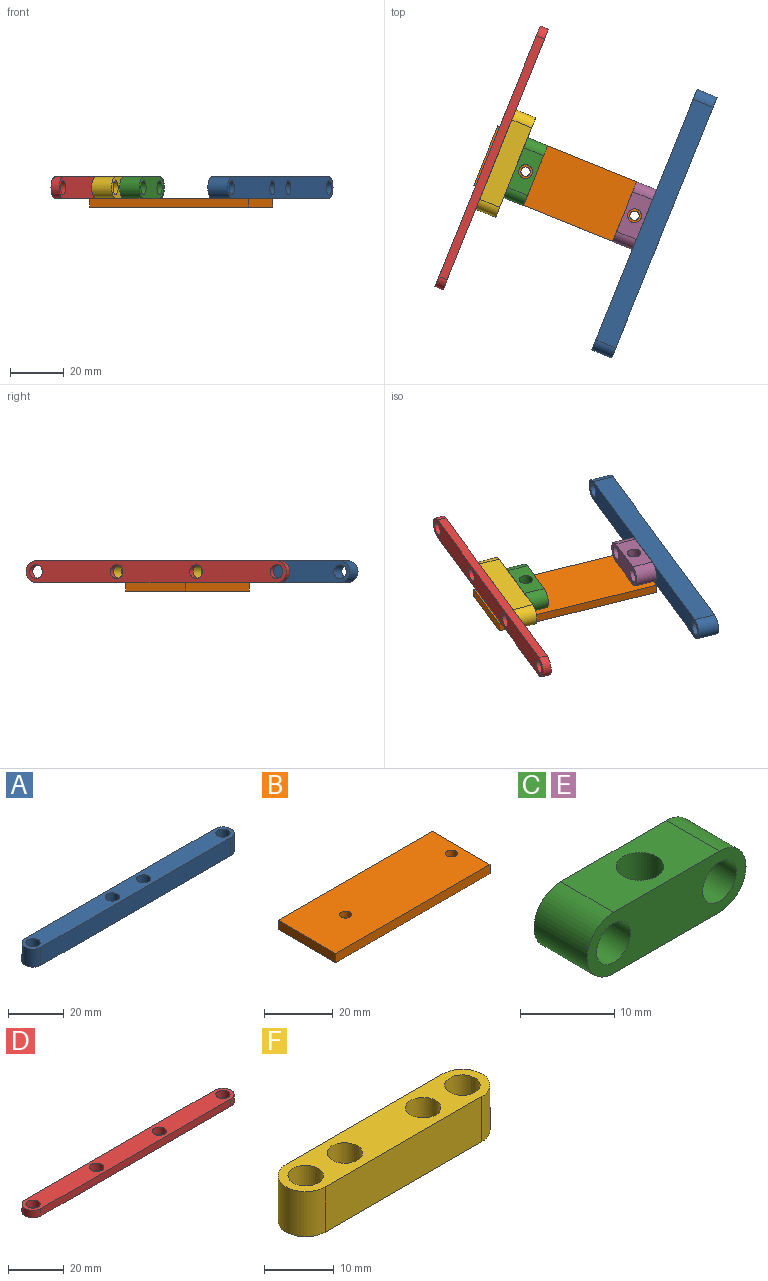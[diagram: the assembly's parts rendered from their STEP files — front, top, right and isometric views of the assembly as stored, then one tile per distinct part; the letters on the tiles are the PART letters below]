
ASSEMBLY  parts=6 mates=14
PART A: 10 faces, bbox 104.1x7.9x7.9 mm
  f0: plane 96.16x7.94mm, normal (0,1,0), area 763.3mm2, adj f6,f7,f8,f9
  f1: plane 96.16x7.94mm, normal (0,-1,0), area 763.3mm2, adj f6,f7,f8,f9
  f2: cylinder r=2.54mm len=7.94mm, axis (0,0,-1), area 126.7mm2, adj f6,f7
  f3: cylinder r=2.54mm len=7.94mm, axis (0,0,-1), area 126.7mm2, adj f6,f7
  f4: cylinder r=2.54mm len=7.94mm, axis (0,0,-1), area 126.7mm2, adj f6,f7
  f5: cylinder r=2.54mm len=7.94mm, axis (0,0,-1), area 126.7mm2, adj f6,f7
  f6: plane 104.1x7.94mm, normal (0,0,1), area 731.7mm2, adj f0,f1,f2,f3,f4,f5,f8,f9
  f7: plane 104.1x7.94mm, normal (0,0,-1), area 731.7mm2, adj f0,f1,f2,f3,f4,f5,f8,f9
  f8: cylinder r=3.97mm len=7.94mm, axis (0,0,-1), area 99mm2, adj f0,f1,f6,f7
  f9: cylinder r=3.97mm len=7.94mm, axis (0,0,-1), area 99mm2, adj f0,f1,f6,f7
PART B: 8 faces, bbox 63.4x23.8x3.3 mm
  f0: plane 63.39x3.25mm, normal (0,1,0), area 206.1mm2, adj f1,f5,f6,f7
  f1: plane 23.81x3.25mm, normal (-1,0,0), area 77.4mm2, adj f0,f2,f6,f7
  f2: plane 63.39x3.25mm, normal (0,-1,0), area 206.1mm2, adj f1,f5,f6,f7
  f3: cylinder r=1.73mm len=3.45mm, axis (0,0,-1), area 35.3mm2, adj f6,f7
  f4: cylinder r=1.73mm len=3.45mm, axis (0,0,-1), area 35.3mm2, adj f6,f7
  f5: plane 23.81x3.25mm, normal (1,0,0), area 77.4mm2, adj f0,f2,f6,f7
  f6: plane 63.39x23.81mm, normal (0,0,1), area 1490.7mm2, adj f0,f1,f2,f3,f4,f5
  f7: plane 63.39x23.81mm, normal (0,0,-1), area 1490.7mm2, adj f0,f1,f2,f3,f4,f5
PART C: 9 faces, bbox 23.8x7.9x7.9 mm
  f0: plane 23.81x7.94mm, normal (0,-1,0), area 135mm2, adj f3,f4,f5,f6,f7,f8
  f1: plane 23.81x7.94mm, normal (0,1,0), area 135mm2, adj f3,f4,f5,f6,f7,f8
  f2: cylinder r=2.54mm len=7.94mm, axis (0,0,-1), area 126.7mm2, adj f3,f4
  f3: plane 15.88x7.94mm, normal (0,0,1), area 105.7mm2, adj f0,f1,f2,f7,f8
  f4: plane 15.88x7.94mm, normal (0,0,-1), area 105.7mm2, adj f0,f1,f2,f7,f8
  f5: cylinder r=2.54mm len=7.94mm, axis (0,-1,0), area 126.7mm2, adj f0,f1
  f6: cylinder r=2.54mm len=7.94mm, axis (0,-1,0), area 126.7mm2, adj f0,f1
  f7: cylinder r=3.97mm len=7.94mm, axis (0,1,0), area 99mm2, adj f0,f1,f3,f4
  f8: cylinder r=3.97mm len=7.94mm, axis (0,-1,0), area 99mm2, adj f0,f1,f3,f4
PART D: 10 faces, bbox 104.1x7.9x3.3 mm
  f0: plane 96.16x3.25mm, normal (0,1,0), area 312.6mm2, adj f6,f7,f8,f9
  f1: plane 96.16x3.25mm, normal (0,-1,0), area 312.6mm2, adj f6,f7,f8,f9
  f2: cylinder r=2.54mm len=5.08mm, axis (0,0,-1), area 51.9mm2, adj f6,f7
  f3: cylinder r=2.54mm len=5.08mm, axis (0,0,-1), area 51.9mm2, adj f6,f7
  f4: cylinder r=2.54mm len=5.08mm, axis (0,0,-1), area 51.9mm2, adj f6,f7
  f5: cylinder r=2.54mm len=5.08mm, axis (0,0,-1), area 51.9mm2, adj f6,f7
  f6: plane 104.1x7.94mm, normal (0,0,1), area 731.7mm2, adj f0,f1,f2,f3,f4,f5,f8,f9
  f7: plane 104.1x7.94mm, normal (0,0,-1), area 731.7mm2, adj f0,f1,f2,f3,f4,f5,f8,f9
  f8: cylinder r=3.97mm len=7.94mm, axis (0,0,-1), area 40.5mm2, adj f0,f1,f6,f7
  f9: cylinder r=3.97mm len=7.94mm, axis (0,0,-1), area 40.5mm2, adj f0,f1,f6,f7
PART E: same geometry as C
PART F: 10 faces, bbox 39.7x7.9x7.9 mm
  f0: plane 31.75x7.94mm, normal (0,1,0), area 252mm2, adj f6,f7,f8,f9
  f1: plane 31.75x7.94mm, normal (0,-1,0), area 252mm2, adj f6,f7,f8,f9
  f2: cylinder r=2.54mm len=7.94mm, axis (0,0,-1), area 126.7mm2, adj f6,f7
  f3: cylinder r=2.54mm len=7.94mm, axis (0,0,-1), area 126.7mm2, adj f6,f7
  f4: cylinder r=2.54mm len=7.94mm, axis (0,0,-1), area 126.7mm2, adj f6,f7
  f5: cylinder r=2.54mm len=7.94mm, axis (0,0,-1), area 126.7mm2, adj f6,f7
  f6: plane 39.69x7.94mm, normal (0,0,1), area 220.4mm2, adj f0,f1,f2,f3,f4,f5,f8,f9
  f7: plane 39.69x7.94mm, normal (0,0,-1), area 220.4mm2, adj f0,f1,f2,f3,f4,f5,f8,f9
  f8: cylinder r=3.97mm len=7.94mm, axis (0,0,-1), area 99mm2, adj f0,f1,f6,f7
  f9: cylinder r=3.97mm len=7.94mm, axis (0,0,-1), area 99mm2, adj f0,f1,f6,f7
PLACE A rot(axis=(0.43,-0.64,-0.64),133.4deg) t=(86.36,34.76,-41.37)mm
PLACE B rot(axis=(0,0,-1),22deg) t=(5.19,24.27,-52.56)mm
PLACE C rot(axis=(0,0,1),68deg) t=(15.45,7.28,-49.31)mm
PLACE D rot(axis=(0.43,-0.64,-0.64),133.4deg) t=(23.91,60,-41.37)mm
PLACE E rot(axis=(0,0,-1),112deg) t=(55.82,-9.04,-49.31)mm
PLACE F rot(axis=(-0.72,-0.49,0.49),108.2deg) t=(4.33,-9.63,-49.31)mm
MATE planar B.f6 <-> A.f1  axis (0,0,1) through (30.04,1.38,-49.31)mm
MATE cylindrical F.f2 <-> C.f8  axis (0.93,-0.37,0) through (7.38,19.1,-45.34)mm
MATE cylindrical B.f3 <-> C.f2  axis (0,0,-1) through (15.45,7.28,-50.93)mm
MATE planar E.f1 <-> B.f5  axis (0.93,-0.37,0) through (59.5,-10.52,-45.34)mm
MATE planar D.f7 <-> F.f6  axis (0.93,-0.37,0) through (4.41,11.74,-45.34)mm
MATE cylindrical E.f7 <-> A.f3  axis (-0.93,0.37,0) through (55.11,-0.19,-45.34)mm
MATE cylindrical F.f3 <-> C.f7  axis (0.93,-0.37,0) through (5.11,2.89,-45.34)mm
MATE cylindrical D.f2 <-> F.f4  axis (0.93,-0.37,0) through (-3.05,-2.37,-45.34)mm
MATE cylindrical B.f4 <-> E.f2  axis (0,0,-1) through (55.82,-9.04,-50.93)mm
MATE cylindrical D.f3 <-> F.f5  axis (0.93,-0.37,0) through (8.85,27.07,-45.34)mm
MATE planar F.f7 <-> C.f1  axis (0.93,-0.37,0) through (11.77,8.77,-45.34)mm
MATE cylindrical C.f7 <-> E.f8  axis (-0.93,0.37,0) through (12.47,-0.08,-45.34)mm
MATE planar A.f6 <-> E.f1  axis (-0.93,0.37,0) through (59.5,-10.52,-45.34)mm
MATE cylindrical A.f2 <-> E.f8  axis (0.93,-0.37,0) through (56.53,-17.88,-45.34)mm
